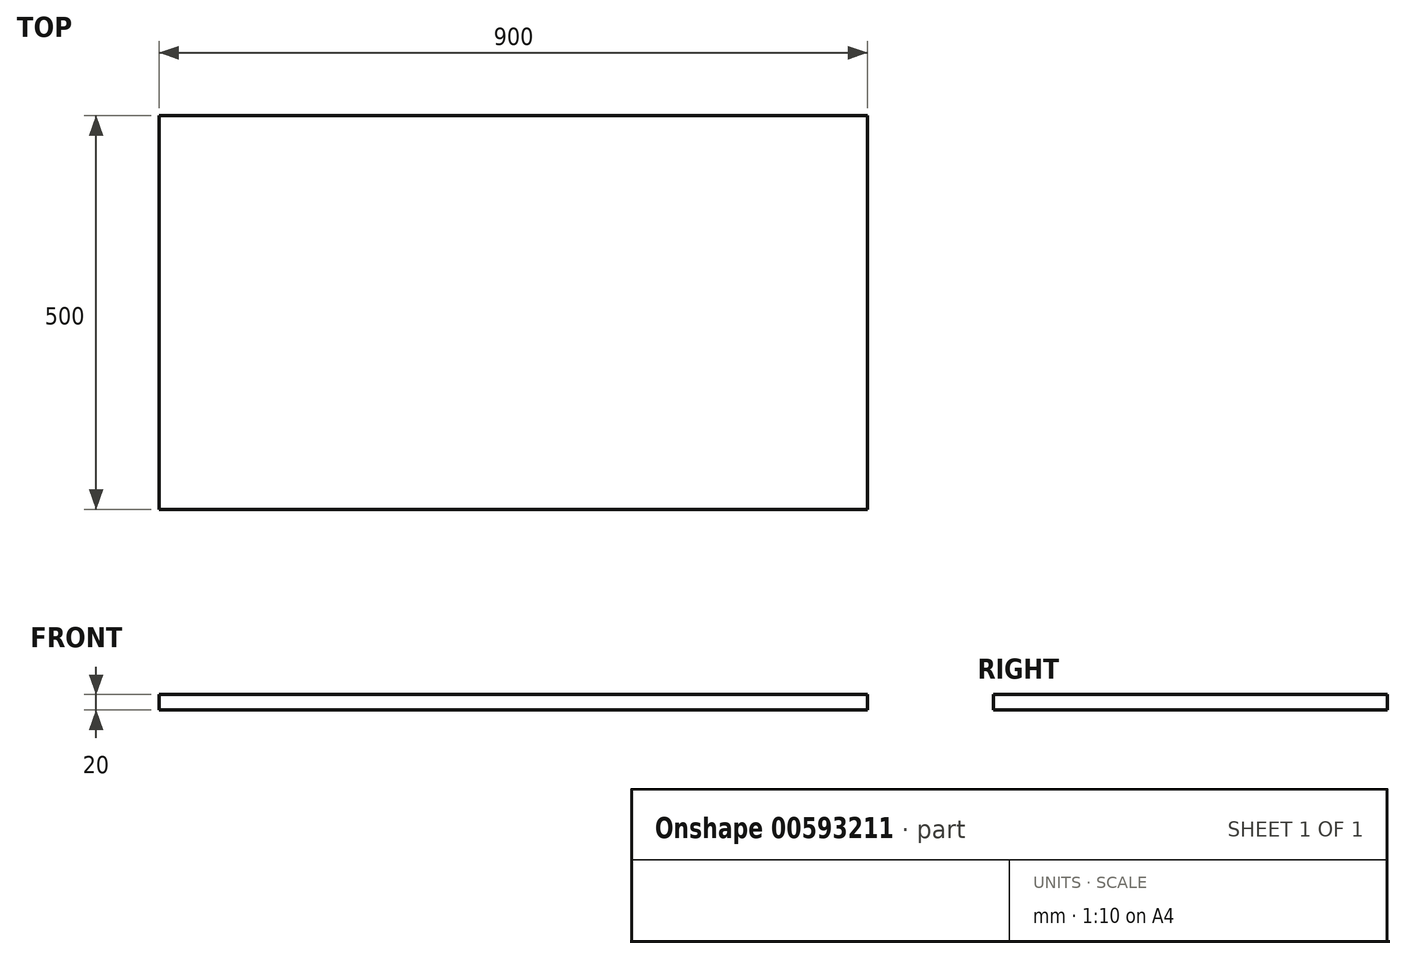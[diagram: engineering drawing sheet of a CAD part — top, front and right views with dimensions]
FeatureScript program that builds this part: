
annotation { "Feature Type Name" : "Feature", "Feature Type Description" : "" }
export const myFeature = defineFeature(function(context is Context, id is Id, definition is map)
    precondition{}
    {
        {
            var Q0;
            Q0=qCreatedBy(makeId("Top.planeOp"),FACE);
            var sketch = newSketch(context, id + "F0", { "sketchPlane" : qUnion([Q0])});
            skLineSegment(sketch, "E0.bottom", {"start": v(-450, 250) * mm, "end": v(450, 250) * mm});
            skLineSegment(sketch, "E0.top", {"start": v(-450, -250) * mm, "end": v(450, -250) * mm});
            skLineSegment(sketch, "E0.left", {"start": v(-450, 250) * mm, "end": v(-450, -250) * mm});
            skLineSegment(sketch, "E0.right", {"start": v(450, 250) * mm, "end": v(450, -250) * mm});
            skPoint(sketch, "E0.middle", {"position": v(0, 0) * mm});
            skSolve(sketch);
        }
        {
            var Q0;
            Q0=makeQuery(id+"F0.imprint","IMPRINT",FACE,{"disambiguationData":[TD([[makeQuery(id+"F0.imprint","IMPRINT",EDGE,{"derivedFrom":sQuery(id+"F0.wireOp",EDGE,"E0.bottom")}),-1.0]])]});
            extrude(context, id + "F1", {"entities" : qUnion([Q0]), "endBound" : BoundingType.SYMMETRIC, "depth" : 20 * mm, "offsetDistance" : 25 * mm});
        }
    });
